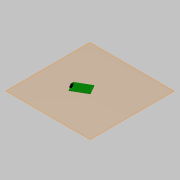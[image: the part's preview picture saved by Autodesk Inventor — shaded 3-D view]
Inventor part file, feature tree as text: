
AUTODESK INVENTOR PART (.ipt)
format: ipt  version: 2014 (Build 180170000, 170)  size: 216,064 bytes
history: native  units: mm
features: extrude x7, sketch x7, reference x2, plane x1, chamfer x1
ambient origin geometry x8: Origin, YZ Plane, XZ Plane, XY Plane, X Axis, Y Axis, Z Axis, Center Point
bodies: Solid1 (feature_tree), Solid2 (feature_tree)
feature tree (18):
  plane  "Work Plane1"
  extrude  "Extrusion1"  Depth=145.0mm
  extrude  "Extrusion2"  Depth=67.5mm
  extrude  "Extrusion3"  Depth=3.0mm
  extrude  "Extrusion4"  Depth=3.0mm
  extrude  "Extrusion5"  Depth=5.0mm
  extrude  "Extrusion6"  Depth=5.0mm
  chamfer  "Chamfer1"  Distance=5.0mm
  extrude  "Extrusion11"  Depth=5.0mm
  sketch  "Sketch1"  dims[d3=100.0mm d4=145.0mm]
  reference  "Reference1"
  reference  "Reference2"
  sketch  "Sketch2"  dims[d5=67.5mm d6=20.0mm]
  sketch  "Sketch3"  dims[d7=3.0mm d8=3.0mm]
  sketch  "Sketch4"  dims[d9=3.0mm d10=3.0mm]
  sketch  "Sketch5"  dims[d11=5.0mm d12=5.0mm]
  sketch  "Sketch6"  dims[d13=5.0mm d14=5.0mm]
  sketch  "Sketch11"  dims[d15=5.0mm d16=5.0mm d17=5.0mm d18=5.0mm d19=16.2mm d20=38.6mm d21=56.8mm d22=1.8mm d23=0.0mm d24=16.2mm d25=38.6mm d26=56.8mm d27=14.4mm d28=13.5mm d29=17.4mm d30=9.2mm d31=9.2mm d32=6.1mm d33=6.1mm d34=8.0mm d35=8.0mm d36=10.5mm d37=0.0mm d38=4.0mm d39=0.0mm d40=13.0mm d41=3.0mm d42=0.0mm d43=3.0mm d44=0.0mm d45=1.5mm d46=10.0mm d47=0.0mm d48=2.0mm d49=2.0mm d50=45.0deg d61=1.0mm d62=0.0mm]
